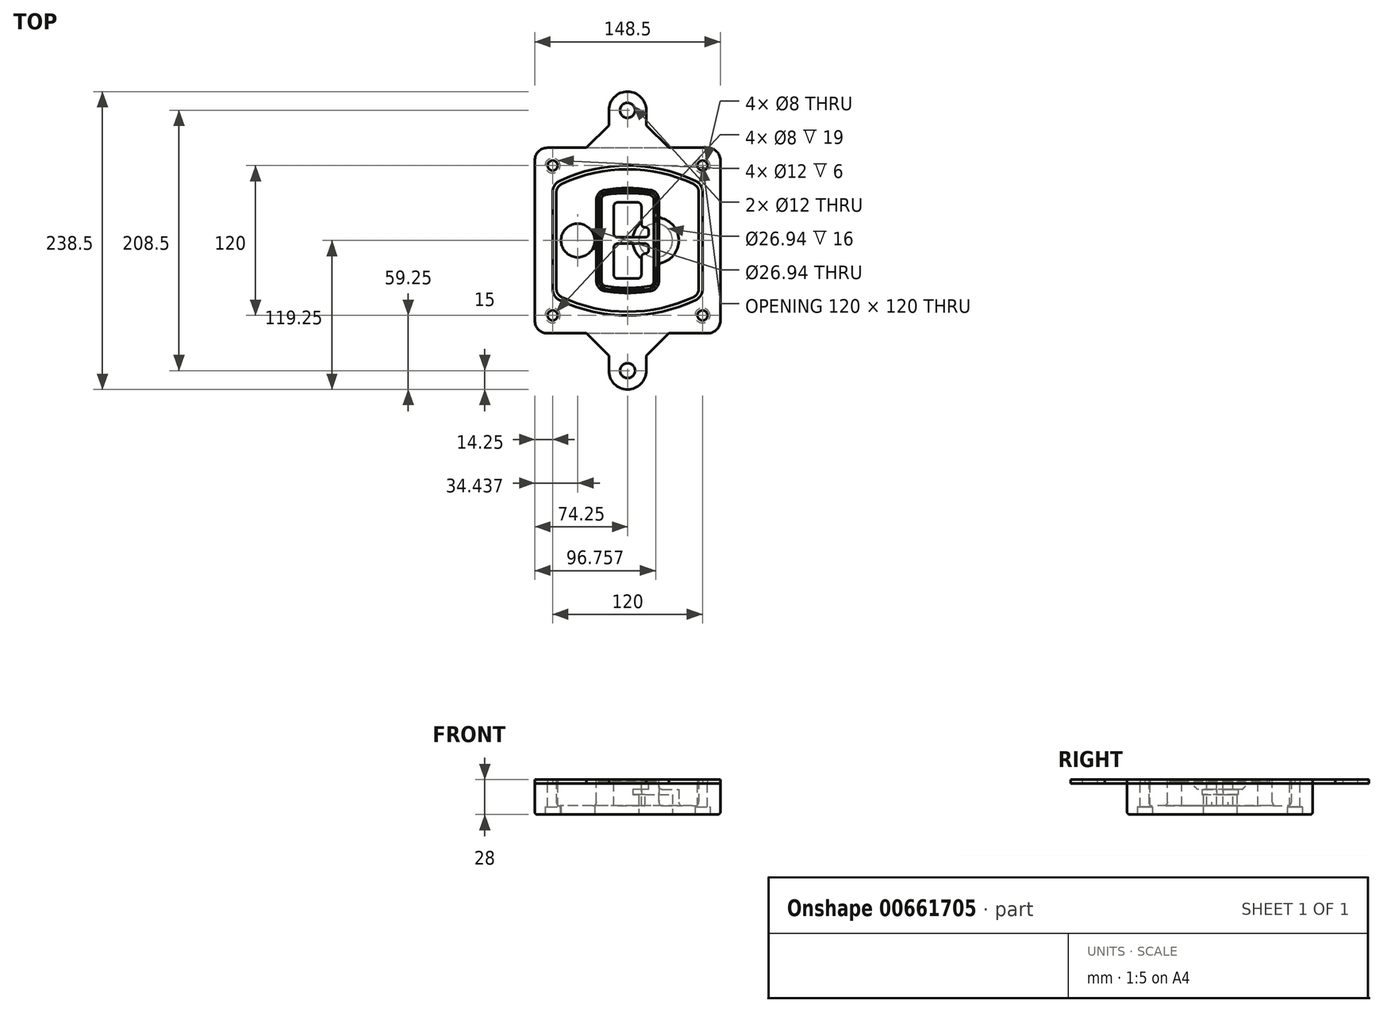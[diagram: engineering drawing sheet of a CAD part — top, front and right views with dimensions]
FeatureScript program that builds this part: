
annotation { "Feature Type Name" : "Feature", "Feature Type Description" : "" }
export const myFeature = defineFeature(function(context is Context, id is Id, definition is map)
    precondition{}
    {
        {
            var Q0;
            Q0=qCreatedBy(makeId("Top.planeOp"),FACE);
            var sketch = newSketch(context, id + "F0", { "sketchPlane" : qUnion([Q0])});
            skPoint(sketch, "E0.rect.middle", {"position": v(0, 0) * mm});
            skLineSegment(sketch, "E1.bottom", {"start": v(-64.25, -74.25) * mm, "end": v(64.25, -74.25) * mm});
            skLineSegment(sketch, "E1.top", {"start": v(-64.25, 74.25) * mm, "end": v(64.25, 74.25) * mm});
            skLineSegment(sketch, "E1.left", {"start": v(-74.25, -64.25) * mm, "end": v(-74.25, 64.25) * mm});
            skLineSegment(sketch, "E1.right", {"start": v(74.25, -64.25) * mm, "end": v(74.25, 64.25) * mm});
            skLineSegment(sketch, "E2", {"start": v(-74.25, 74.25) * mm, "end": v(74.25, -74.25) * mm, "construction": true});
            skLineSegment(sketch, "E3", {"start": v(74.25, 74.25) * mm, "end": v(-74.25, -74.25) * mm, "construction": true});
            skCircle(sketch, "E4", {"center": v(-60, 60) * mm, "radius": 4 * mm});
            skCircle(sketch, "E5", {"center": v(60, 60) * mm, "radius": 4 * mm});
            skCircle(sketch, "E6", {"center": v(60, -60) * mm, "radius": 4 * mm});
            skCircle(sketch, "E7", {"center": v(-60, -60) * mm, "radius": 4 * mm});
            skLineSegment(sketch, "E8", {"start": v(-60, 60) * mm, "end": v(60, 60) * mm, "construction": true});
            skLineSegment(sketch, "E9", {"start": v(60, 60) * mm, "end": v(60, -60) * mm, "construction": true});
            skLineSegment(sketch, "E10", {"start": v(60, -60) * mm, "end": v(-60, -60) * mm, "construction": true});
            skLineSegment(sketch, "E11", {"start": v(-60, -60) * mm, "end": v(-60, 60) * mm, "construction": true});
            skLineSegment(sketch, "E12", {"start": v(-60, 38.83) * mm, "end": v(-60, -38.83) * mm});
            skLineSegment(sketch, "E13", {"start": v(60, 38.83) * mm, "end": v(60, -38.83) * mm});
            skArc(sketch, "E14", {"start": v(54.26, 47.88) * mm, "mid": v(0, 60) * mm, "end": v(-54.26, 47.88) * mm});
            skArc(sketch, "E15", {"start": v(-54.26, -47.88) * mm, "mid": v(0, -60) * mm, "end": v(54.26, -47.88) * mm});
            skLineSegment(sketch, "E16", {"start": v(-60, 0) * mm, "end": v(60, 0) * mm, "construction": true});
            skPoint(sketch, "E17.visualSharp", {"position": v(-60, -45) * mm});
            skArc(sketch, "E17.filletArc", {"start": v(-60, -38.83) * mm, "mid": v(-58.44, -44.2) * mm, "end": v(-54.26, -47.88) * mm});
            skPoint(sketch, "E18.visualSharp", {"position": v(-60, 45) * mm});
            skArc(sketch, "E18.filletArc", {"start": v(-54.26, 47.88) * mm, "mid": v(-58.44, 44.2) * mm, "end": v(-60, 38.83) * mm});
            skPoint(sketch, "E19.visualSharp", {"position": v(60, 45) * mm});
            skArc(sketch, "E19.filletArc", {"start": v(60, 38.83) * mm, "mid": v(58.44, 44.2) * mm, "end": v(54.26, 47.88) * mm});
            skPoint(sketch, "E20.visualSharp", {"position": v(60, -45) * mm});
            skArc(sketch, "E20.filletArc", {"start": v(54.26, -47.88) * mm, "mid": v(58.44, -44.2) * mm, "end": v(60, -38.83) * mm});
            skPoint(sketch, "E21.visualSharp", {"position": v(-74.25, 74.25) * mm});
            skArc(sketch, "E21.filletArc", {"start": v(-64.25, 74.25) * mm, "mid": v(-71.32, 71.32) * mm, "end": v(-74.25, 64.25) * mm});
            skPoint(sketch, "E22.visualSharp", {"position": v(74.25, 74.25) * mm});
            skArc(sketch, "E22.filletArc", {"start": v(74.25, 64.25) * mm, "mid": v(71.32, 71.32) * mm, "end": v(64.25, 74.25) * mm});
            skPoint(sketch, "E23.visualSharp", {"position": v(74.25, -74.25) * mm});
            skArc(sketch, "E23.filletArc", {"start": v(64.25, -74.25) * mm, "mid": v(71.32, -71.32) * mm, "end": v(74.25, -64.25) * mm});
            skPoint(sketch, "E24.visualSharp", {"position": v(-74.25, -74.25) * mm});
            skArc(sketch, "E24.filletArc", {"start": v(-74.25, -64.25) * mm, "mid": v(-71.32, -71.32) * mm, "end": v(-64.25, -74.25) * mm});
            skArc(sketch, "E25.0", {"start": v(57, 38.83) * mm, "mid": v(55.9, 42.58) * mm, "end": v(52.98, 45.17) * mm});
            skLineSegment(sketch, "E25.1", {"start": v(57, 38.83) * mm, "end": v(57, -38.83) * mm});
            skArc(sketch, "E25.2", {"start": v(52.98, -45.17) * mm, "mid": v(55.9, -42.58) * mm, "end": v(57, -38.83) * mm});
            skArc(sketch, "E25.3", {"start": v(-52.98, -45.17) * mm, "mid": v(0, -57) * mm, "end": v(52.98, -45.17) * mm});
            skArc(sketch, "E25.4", {"start": v(-57, -38.83) * mm, "mid": v(-55.9, -42.58) * mm, "end": v(-52.98, -45.17) * mm});
            skArc(sketch, "E25.5", {"start": v(52.98, 45.17) * mm, "mid": v(0, 57) * mm, "end": v(-52.98, 45.17) * mm});
            skLineSegment(sketch, "E25.6", {"start": v(-57, 38.83) * mm, "end": v(-57, -38.83) * mm});
            skArc(sketch, "E25.7", {"start": v(-52.98, 45.17) * mm, "mid": v(-55.9, 42.58) * mm, "end": v(-57, 38.83) * mm});
            skArc(sketch, "E26.0", {"start": v(-55.96, 51.5) * mm, "mid": v(-61.82, 46.33) * mm, "end": v(-64, 38.83) * mm});
            skArc(sketch, "E26.1", {"start": v(55.96, 51.5) * mm, "mid": v(0, 64) * mm, "end": v(-55.96, 51.5) * mm});
            skArc(sketch, "E26.2", {"start": v(64, 38.83) * mm, "mid": v(61.82, 46.33) * mm, "end": v(55.96, 51.5) * mm});
            skLineSegment(sketch, "E26.3", {"start": v(64, 38.83) * mm, "end": v(64, -38.83) * mm});
            skArc(sketch, "E26.4", {"start": v(55.96, -51.5) * mm, "mid": v(61.82, -46.33) * mm, "end": v(64, -38.83) * mm});
            skLineSegment(sketch, "E26.5", {"start": v(-64, 38.83) * mm, "end": v(-64, -38.83) * mm});
            skArc(sketch, "E26.6", {"start": v(-55.96, -51.5) * mm, "mid": v(0, -64) * mm, "end": v(55.96, -51.5) * mm});
            skArc(sketch, "E26.7", {"start": v(-64, -38.83) * mm, "mid": v(-61.82, -46.33) * mm, "end": v(-55.96, -51.5) * mm});
            skSolve(sketch);
        }
        {
            var Q0;
            Q0=makeQuery(id+"F0.imprint","IMPRINT",FACE,{"disambiguationData":[TD([[makeQuery(id+"F0.imprint","IMPRINT",EDGE,{"derivedFrom":sQuery(id+"F0.wireOp",EDGE,"E1.bottom")}),1.0]])]});
            var Q1;
            Q1=makeQuery(id+"F0.imprint","IMPRINT",FACE,{"disambiguationData":[TD([[makeQuery(id+"F0.imprint","IMPRINT",EDGE,{"derivedFrom":sQuery(id+"F0.wireOp",EDGE,"E12")}),1.0]])]});
            var Q2;
            Q2=makeQuery(id+"F0.imprint","IMPRINT",FACE,{"disambiguationData":[TD([[makeQuery(id+"F0.imprint","IMPRINT",EDGE,{"derivedFrom":sQuery(id+"F0.wireOp",EDGE,"E25.0")}),1.0]])]});
            var Q3;
            Q3=makeQuery(id+"F0.imprint","IMPRINT",FACE,{"disambiguationData":[TD([[makeQuery(id+"F0.imprint","IMPRINT",EDGE,{"derivedFrom":sQuery(id+"F0.wireOp",EDGE,"E12")}),-1.0]])]});
            extrude(context, id + "F1", {"entities" : qUnion([Q0, Q1, Q2, Q3]), "oppositeDirection" : true, "depth" : 25 * mm});
        }
        {
            var Q0;
            Q0=makeQuery(id+"F0.imprint","IMPRINT",FACE,{"disambiguationData":[TD([[makeQuery(id+"F0.imprint","IMPRINT",EDGE,{"derivedFrom":sQuery(id+"F0.wireOp",EDGE,"E12")}),1.0]])]});
            extrude(context, id + "F2", {"entities" : qUnion([Q0]), "operationType" : NewBodyOperationType.ADD, "depth" : 3 * mm});
        }
        {
            var Q0;
            Q0=makeQuery(id+"F0.imprint","IMPRINT",FACE,{"disambiguationData":[TD([[makeQuery(id+"F0.imprint","IMPRINT",EDGE,{"derivedFrom":sQuery(id+"F0.wireOp",EDGE,"E25.0")}),1.0]])]});
            extrude(context, id + "F3", {"entities" : qUnion([Q0]), "operationType" : NewBodyOperationType.REMOVE, "oppositeDirection" : true, "depth" : 18 * mm});
        }
        {
            var Q0;
            Q0=makeQuery(id+"F2.opExtrude","CAP_FACE",FACE,{"disambiguationData":[OSD([sQuery(id+"F0.wireOp",EDGE,"E12"),sQuery(id+"F0.wireOp",EDGE,"E13"),sQuery(id+"F0.wireOp",EDGE,"E14"),sQuery(id+"F0.wireOp",EDGE,"E15"),sQuery(id+"F0.wireOp",EDGE,"E17.filletArc"),sQuery(id+"F0.wireOp",EDGE,"E18.filletArc"),sQuery(id+"F0.wireOp",EDGE,"E19.filletArc"),sQuery(id+"F0.wireOp",EDGE,"E20.filletArc"),sQuery(id+"F0.wireOp",EDGE,"E25.0"),sQuery(id+"F0.wireOp",EDGE,"E25.1"),sQuery(id+"F0.wireOp",EDGE,"E25.2"),sQuery(id+"F0.wireOp",EDGE,"E25.3"),sQuery(id+"F0.wireOp",EDGE,"E25.4"),sQuery(id+"F0.wireOp",EDGE,"E25.5"),sQuery(id+"F0.wireOp",EDGE,"E25.6"),sQuery(id+"F0.wireOp",EDGE,"E25.7")])],"isStart":false});
            var sketch = newSketch(context, id + "F4", { "sketchPlane" : qUnion([Q0])});
            skArc(sketch, "E27.0", {"start": v(-18.34, -40.45) * mm, "mid": v(0, -42) * mm, "end": v(18.34, -40.45) * mm});
            skArc(sketch, "E28.0", {"start": v(18.34, 40.45) * mm, "mid": v(0, 42) * mm, "end": v(-18.34, 40.45) * mm});
            skLineSegment(sketch, "E29", {"start": v(-25, 32.57) * mm, "end": v(-25, -32.57) * mm});
            skLineSegment(sketch, "E30", {"start": v(25, 32.57) * mm, "end": v(25, -32.57) * mm});
            skLineSegment(sketch, "E31", {"start": v(-25, 39.1) * mm, "end": v(25, 39.1) * mm, "construction": true});
            skLineSegment(sketch, "E32", {"start": v(-25, -39.1) * mm, "end": v(25, -39.1) * mm, "construction": true});
            skPoint(sketch, "E33.visualSharp", {"position": v(-25, 39.1) * mm});
            skArc(sketch, "E33.filletArc", {"start": v(-18.34, 40.45) * mm, "mid": v(-23.11, 37.73) * mm, "end": v(-25, 32.57) * mm});
            skPoint(sketch, "E34.visualSharp", {"position": v(25, 39.1) * mm});
            skArc(sketch, "E34.filletArc", {"start": v(25, 32.57) * mm, "mid": v(23.11, 37.73) * mm, "end": v(18.34, 40.45) * mm});
            skPoint(sketch, "E35.visualSharp", {"position": v(25, -39.1) * mm});
            skArc(sketch, "E35.filletArc", {"start": v(18.34, -40.45) * mm, "mid": v(23.11, -37.73) * mm, "end": v(25, -32.57) * mm});
            skPoint(sketch, "E36.visualSharp", {"position": v(-25, -39.1) * mm});
            skArc(sketch, "E36.filletArc", {"start": v(-25, -32.57) * mm, "mid": v(-23.11, -37.73) * mm, "end": v(-18.34, -40.45) * mm});
            skArc(sketch, "E37.0", {"start": v(52.98, 45.17) * mm, "mid": v(0, 57) * mm, "end": v(-52.98, 45.17) * mm});
            skArc(sketch, "E37.1", {"start": v(-52.98, 45.17) * mm, "mid": v(-55.9, 42.58) * mm, "end": v(-57, 38.83) * mm});
            skLineSegment(sketch, "E37.2", {"start": v(-57, 38.83) * mm, "end": v(-57, -38.83) * mm});
            skArc(sketch, "E37.3", {"start": v(-57, -38.83) * mm, "mid": v(-55.9, -42.58) * mm, "end": v(-52.98, -45.17) * mm});
            skArc(sketch, "E37.4", {"start": v(-52.98, -45.17) * mm, "mid": v(0, -57) * mm, "end": v(52.98, -45.17) * mm});
            skArc(sketch, "E37.5", {"start": v(52.98, -45.17) * mm, "mid": v(55.9, -42.58) * mm, "end": v(57, -38.83) * mm});
            skLineSegment(sketch, "E37.6", {"start": v(57, 38.83) * mm, "end": v(57, -38.83) * mm});
            skArc(sketch, "E37.7", {"start": v(57, 38.83) * mm, "mid": v(55.9, 42.58) * mm, "end": v(52.98, 45.17) * mm});
            skLineSegment(sketch, "E38.0", {"start": v(23, 32.57) * mm, "end": v(23, -32.57) * mm});
            skArc(sketch, "E38.1", {"start": v(18, -38.48) * mm, "mid": v(21.58, -36.44) * mm, "end": v(23, -32.57) * mm});
            skArc(sketch, "E38.2", {"start": v(-18, -38.48) * mm, "mid": v(0, -40) * mm, "end": v(18, -38.48) * mm});
            skArc(sketch, "E38.3", {"start": v(-23, -32.57) * mm, "mid": v(-21.58, -36.44) * mm, "end": v(-18, -38.48) * mm});
            skLineSegment(sketch, "E38.4", {"start": v(-23, 32.57) * mm, "end": v(-23, -32.57) * mm});
            skArc(sketch, "E38.5", {"start": v(23, 32.57) * mm, "mid": v(21.58, 36.44) * mm, "end": v(18, 38.48) * mm});
            skArc(sketch, "E38.6", {"start": v(-18, 38.48) * mm, "mid": v(-21.58, 36.44) * mm, "end": v(-23, 32.57) * mm});
            skArc(sketch, "E38.7", {"start": v(18, 38.48) * mm, "mid": v(0, 40) * mm, "end": v(-18, 38.48) * mm});
            skArc(sketch, "E39.0", {"start": v(21, 32.57) * mm, "mid": v(20.06, 35.15) * mm, "end": v(17.67, 36.5) * mm});
            skLineSegment(sketch, "E39.1", {"start": v(21, 32.57) * mm, "end": v(21, -32.57) * mm});
            skArc(sketch, "E39.2", {"start": v(17.67, -36.5) * mm, "mid": v(20.06, -35.15) * mm, "end": v(21, -32.57) * mm});
            skArc(sketch, "E39.3", {"start": v(-17.67, -36.5) * mm, "mid": v(0, -38) * mm, "end": v(17.67, -36.5) * mm});
            skArc(sketch, "E39.4", {"start": v(-21, -32.57) * mm, "mid": v(-20.06, -35.15) * mm, "end": v(-17.67, -36.5) * mm});
            skArc(sketch, "E39.5", {"start": v(17.67, 36.5) * mm, "mid": v(0, 38) * mm, "end": v(-17.67, 36.5) * mm});
            skLineSegment(sketch, "E39.6", {"start": v(-21, 32.57) * mm, "end": v(-21, -32.57) * mm});
            skArc(sketch, "E39.7", {"start": v(-17.67, 36.5) * mm, "mid": v(-20.06, 35.15) * mm, "end": v(-21, 32.57) * mm});
            skLineSegment(sketch, "E40", {"start": v(-25, 0) * mm, "end": v(25, 0) * mm, "construction": true});
            skLineSegment(sketch, "E41", {"start": v(-11, 5.5) * mm, "end": v(-11, 27.5) * mm});
            skLineSegment(sketch, "E42", {"start": v(-8, 30.5) * mm, "end": v(8, 30.5) * mm});
            skLineSegment(sketch, "E43", {"start": v(11, 27.5) * mm, "end": v(11, 13.5) * mm});
            skLineSegment(sketch, "E44", {"start": v(14, 10.5) * mm, "end": v(14, 10.5) * mm});
            skLineSegment(sketch, "E45", {"start": v(17, 7.5) * mm, "end": v(17, 5.5) * mm});
            skLineSegment(sketch, "E46", {"start": v(14, 2.5) * mm, "end": v(-8, 2.5) * mm});
            skPoint(sketch, "E47.visualSharp", {"position": v(-11, 30.5) * mm});
            skArc(sketch, "E47.filletArc", {"start": v(-8, 30.5) * mm, "mid": v(-10.12, 29.62) * mm, "end": v(-11, 27.5) * mm});
            skPoint(sketch, "E48.visualSharp", {"position": v(11, 30.5) * mm});
            skArc(sketch, "E48.filletArc", {"start": v(11, 27.5) * mm, "mid": v(10.12, 29.62) * mm, "end": v(8, 30.5) * mm});
            skPoint(sketch, "E49.visualSharp", {"position": v(11, 10.5) * mm});
            skArc(sketch, "E49.filletArc", {"start": v(11, 13.5) * mm, "mid": v(11.88, 11.38) * mm, "end": v(14, 10.5) * mm});
            skPoint(sketch, "E50.visualSharp", {"position": v(17, 10.5) * mm});
            skArc(sketch, "E50.filletArc", {"start": v(17, 7.5) * mm, "mid": v(16.12, 9.62) * mm, "end": v(14, 10.5) * mm});
            skPoint(sketch, "E51.visualSharp", {"position": v(17, 2.5) * mm});
            skArc(sketch, "E51.filletArc", {"start": v(14, 2.5) * mm, "mid": v(16.12, 3.38) * mm, "end": v(17, 5.5) * mm});
            skPoint(sketch, "E52.visualSharp", {"position": v(-11, 2.5) * mm});
            skArc(sketch, "E52.filletArc", {"start": v(-11, 5.5) * mm, "mid": v(-10.12, 3.38) * mm, "end": v(-8, 2.5) * mm});
            skLineSegment(sketch, "E53.0.MirrorCS", {"start": v(14, -2.5) * mm, "end": v(-8, -2.5) * mm});
            skArc(sketch, "E54.0.MirrorCS", {"start": v(-11, -5.5) * mm, "mid": v(-10.12, -3.38) * mm, "end": v(-8, -2.5) * mm});
            skLineSegment(sketch, "E55.0.MirrorCS", {"start": v(-11, -5.5) * mm, "end": v(-11, -27.5) * mm});
            skArc(sketch, "E56.0.MirrorCS", {"start": v(-8, -30.5) * mm, "mid": v(-10.12, -29.62) * mm, "end": v(-11, -27.5) * mm});
            skLineSegment(sketch, "E57.0.MirrorCS", {"start": v(-8, -30.5) * mm, "end": v(8, -30.5) * mm});
            skArc(sketch, "E58.0.MirrorCS", {"start": v(11, -27.5) * mm, "mid": v(10.12, -29.62) * mm, "end": v(8, -30.5) * mm});
            skLineSegment(sketch, "E59.0.MirrorCS", {"start": v(11, -27.5) * mm, "end": v(11, -13.5) * mm});
            skArc(sketch, "E60.0.MirrorCS", {"start": v(11, -13.5) * mm, "mid": v(11.88, -11.38) * mm, "end": v(14, -10.5) * mm});
            skArc(sketch, "E61.0.MirrorCS", {"start": v(17, -7.5) * mm, "mid": v(16.12, -9.62) * mm, "end": v(14, -10.5) * mm});
            skLineSegment(sketch, "E62.0.MirrorCS", {"start": v(17, -7.5) * mm, "end": v(17, -5.5) * mm});
            skArc(sketch, "E63.0.MirrorCS", {"start": v(14, -2.5) * mm, "mid": v(16.12, -3.38) * mm, "end": v(17, -5.5) * mm});
            skSolve(sketch);
        }
        {
            var Q0;
            Q0=makeQuery(id+"F4.imprint","IMPRINT",FACE,{"disambiguationData":[TD([[makeQuery(id+"F4.imprint","IMPRINT",EDGE,{"derivedFrom":sQuery(id+"F4.wireOp",EDGE,"E27.0")}),1.0]])]});
            var Q1;
            Q1=makeQuery(id+"F4.imprint","IMPRINT",FACE,{"disambiguationData":[TD([[makeQuery(id+"F4.imprint","IMPRINT",EDGE,{"derivedFrom":sQuery(id+"F4.wireOp",EDGE,"E38.0")}),-1.0]])]});
            var Q2;
            Q2=makeQuery(id+"F4.imprint","IMPRINT",FACE,{"disambiguationData":[TD([[makeQuery(id+"F4.imprint","IMPRINT",EDGE,{"derivedFrom":sQuery(id+"F4.wireOp",EDGE,"E39.0")}),1.0]])]});
            extrude(context, id + "F5", {"entities" : qUnion([Q0, Q1, Q2]), "operationType" : NewBodyOperationType.ADD, "endBound" : BoundingType.UP_TO_NEXT, "oppositeDirection" : true, "depth" : 25 * mm});
        }
        {
            var Q0;
            Q0=makeQuery(id+"F4.imprint","IMPRINT",FACE,{"disambiguationData":[TD([[makeQuery(id+"F4.imprint","IMPRINT",EDGE,{"derivedFrom":sQuery(id+"F4.wireOp",EDGE,"E38.0")}),-1.0]])]});
            extrude(context, id + "F6", {"entities" : qUnion([Q0]), "operationType" : NewBodyOperationType.REMOVE, "oppositeDirection" : true, "depth" : 2 * mm});
        }
        {
            var Q0;
            Q0=makeQuery(id+"F1.opExtrude","CAP_FACE",FACE,{"disambiguationData":[OSD([sQuery(id+"F0.wireOp",EDGE,"E1.bottom"),sQuery(id+"F0.wireOp",EDGE,"E1.top"),sQuery(id+"F0.wireOp",EDGE,"E1.left"),sQuery(id+"F0.wireOp",EDGE,"E1.right"),sQuery(id+"F0.wireOp",EDGE,"E4"),sQuery(id+"F0.wireOp",EDGE,"E5"),sQuery(id+"F0.wireOp",EDGE,"E6"),sQuery(id+"F0.wireOp",EDGE,"E7"),sQuery(id+"F0.wireOp",EDGE,"E21.filletArc"),sQuery(id+"F0.wireOp",EDGE,"E22.filletArc"),sQuery(id+"F0.wireOp",EDGE,"E23.filletArc"),sQuery(id+"F0.wireOp",EDGE,"E24.filletArc")])],"isStart":false});
            var sketch = newSketch(context, id + "F7", { "sketchPlane" : qUnion([Q0])});
            skCircle(sketch, "E64", {"center": v(22.5, 0) * mm, "radius": 13.47 * mm});
            skCircle(sketch, "E65", {"center": v(-39.81, 0) * mm, "radius": 13.47 * mm});
            skLineSegment(sketch, "E66", {"start": v(74.25, 0) * mm, "end": v(-74.25, 0) * mm});
            skCircle(sketch, "E67", {"center": v(22.5, 0) * mm, "radius": 18.47 * mm});
            skCircle(sketch, "E68", {"center": v(60, -60) * mm, "radius": 6 * mm});
            skCircle(sketch, "E69", {"center": v(-60, -60) * mm, "radius": 6 * mm});
            skCircle(sketch, "E70", {"center": v(-60, 60) * mm, "radius": 6 * mm});
            skCircle(sketch, "E71", {"center": v(60, 60) * mm, "radius": 6 * mm});
            skSolve(sketch);
        }
        {
            var Q0;
            {var subQ1=sQuery(id+"F7.wireOp",EDGE,"E66");var subQ4=sQuery(id+"F7.wireOp",EDGE,"E64");var subQ6=makeQuery(id+"F7.imprint","INTERSECT",VERTEX,{"disambiguationData":[OD(0.0)],"derivedFrom":[subQ4,subQ1]});Q0=makeQuery(id+"F7.imprint","IMPRINT",FACE,{"disambiguationData":[TD([[makeQuery(id+"F7.imprint","IMPRINT",EDGE,{"disambiguationData":[TD([[subQ6,-1.0]])],"derivedFrom":subQ4}),-1.0]])]});}
            var Q1;
            {var subQ0=sQuery(id+"F7.wireOp",EDGE,"E66");var subQ1=sQuery(id+"F7.wireOp",EDGE,"E64");var subQ3=makeQuery(id+"F7.imprint","INTERSECT",VERTEX,{"disambiguationData":[OD(0.0)],"derivedFrom":[subQ1,subQ0]});Q1=makeQuery(id+"F7.imprint","IMPRINT",FACE,{"disambiguationData":[TD([[makeQuery(id+"F7.imprint","IMPRINT",EDGE,{"disambiguationData":[TD([[subQ3,-1.0]])],"derivedFrom":subQ1}),1.0]])]});}
            var Q2;
            {var subQ0=sQuery(id+"F7.wireOp",EDGE,"E66");var subQ1=sQuery(id+"F7.wireOp",EDGE,"E64");var subQ3=makeQuery(id+"F7.imprint","INTERSECT",VERTEX,{"disambiguationData":[OD(0.0)],"derivedFrom":[subQ1,subQ0]});Q2=makeQuery(id+"F7.imprint","IMPRINT",FACE,{"disambiguationData":[TD([[makeQuery(id+"F7.imprint","IMPRINT",EDGE,{"disambiguationData":[TD([[subQ3,1.0]])],"derivedFrom":subQ1}),1.0]])]});}
            var Q3;
            {var subQ1=sQuery(id+"F7.wireOp",EDGE,"E66");var subQ4=sQuery(id+"F7.wireOp",EDGE,"E64");var subQ6=makeQuery(id+"F7.imprint","INTERSECT",VERTEX,{"disambiguationData":[OD(0.0)],"derivedFrom":[subQ4,subQ1]});Q3=makeQuery(id+"F7.imprint","IMPRINT",FACE,{"disambiguationData":[TD([[makeQuery(id+"F7.imprint","IMPRINT",EDGE,{"disambiguationData":[TD([[subQ6,1.0]])],"derivedFrom":subQ4}),-1.0]])]});}
            extrude(context, id + "F8", {"entities" : qUnion([Q0, Q1, Q2, Q3]), "operationType" : NewBodyOperationType.ADD, "oppositeDirection" : true, "depth" : 20 * mm});
        }
        {
            var Q0;
            {var subQ0=sQuery(id+"F7.wireOp",EDGE,"E66");var subQ1=sQuery(id+"F7.wireOp",EDGE,"E64");var subQ3=makeQuery(id+"F7.imprint","INTERSECT",VERTEX,{"disambiguationData":[OD(0.0)],"derivedFrom":[subQ1,subQ0]});Q0=makeQuery(id+"F7.imprint","IMPRINT",FACE,{"disambiguationData":[TD([[makeQuery(id+"F7.imprint","IMPRINT",EDGE,{"disambiguationData":[TD([[subQ3,-1.0]])],"derivedFrom":subQ1}),1.0]])]});}
            var Q1;
            {var subQ0=sQuery(id+"F7.wireOp",EDGE,"E66");var subQ1=sQuery(id+"F7.wireOp",EDGE,"E64");var subQ3=makeQuery(id+"F7.imprint","INTERSECT",VERTEX,{"disambiguationData":[OD(0.0)],"derivedFrom":[subQ1,subQ0]});Q1=makeQuery(id+"F7.imprint","IMPRINT",FACE,{"disambiguationData":[TD([[makeQuery(id+"F7.imprint","IMPRINT",EDGE,{"disambiguationData":[TD([[subQ3,1.0]])],"derivedFrom":subQ1}),1.0]])]});}
            var Q2;
            Q2 = qSketchRegion(id + "F16", true);
            extrude(context, id + "F9", {"entities" : qUnion([Q0, Q1, Q2]), "operationType" : NewBodyOperationType.REMOVE, "oppositeDirection" : true, "depth" : 16 * mm, "offsetDistance" : 25 * mm});
        }
        {
            var Q0;
            {var subQ0=sQuery(id+"F7.wireOp",EDGE,"E66");var subQ1=sQuery(id+"F7.wireOp",EDGE,"E65");var subQ3=makeQuery(id+"F7.imprint","INTERSECT",VERTEX,{"disambiguationData":[OD(0.0)],"derivedFrom":[subQ1,subQ0]});Q0=makeQuery(id+"F7.imprint","IMPRINT",FACE,{"disambiguationData":[TD([[makeQuery(id+"F7.imprint","IMPRINT",EDGE,{"disambiguationData":[TD([[subQ3,-1.0]])],"derivedFrom":subQ1}),1.0]])]});}
            var Q1;
            {var subQ0=sQuery(id+"F7.wireOp",EDGE,"E66");var subQ1=sQuery(id+"F7.wireOp",EDGE,"E65");var subQ3=makeQuery(id+"F7.imprint","INTERSECT",VERTEX,{"disambiguationData":[OD(0.0)],"derivedFrom":[subQ1,subQ0]});Q1=makeQuery(id+"F7.imprint","IMPRINT",FACE,{"disambiguationData":[TD([[makeQuery(id+"F7.imprint","IMPRINT",EDGE,{"disambiguationData":[TD([[subQ3,1.0]])],"derivedFrom":subQ1}),1.0]])]});}
            extrude(context, id + "F10", {"entities" : qUnion([Q0, Q1]), "operationType" : NewBodyOperationType.REMOVE, "oppositeDirection" : true, "depth" : 25 * mm});
        }
        {
            var Q0;
            Q0=makeQuery(id+"F7.imprint","IMPRINT",FACE,{"disambiguationData":[TD([[makeQuery(id+"F7.imprint","IMPRINT",EDGE,{"derivedFrom":sQuery(id+"F7.wireOp",EDGE,"E68")}),1.0]])]});
            var Q1;
            Q1=makeQuery(id+"F7.imprint","IMPRINT",FACE,{"disambiguationData":[TD([[makeQuery(id+"F7.imprint","IMPRINT",EDGE,{"derivedFrom":makeQuery(id+"F1.opExtrude","CAP_EDGE",EDGE,{"disambiguationData":[OSD([sQuery(id+"F0.wireOp",EDGE,"E5")])],"isStart":false})}),-1.0]])]});
            var Q2;
            Q2=makeQuery(id+"F7.imprint","IMPRINT",FACE,{"disambiguationData":[TD([[makeQuery(id+"F7.imprint","IMPRINT",EDGE,{"derivedFrom":sQuery(id+"F7.wireOp",EDGE,"E69")}),1.0]])]});
            var Q3;
            Q3=makeQuery(id+"F7.imprint","IMPRINT",FACE,{"disambiguationData":[TD([[makeQuery(id+"F7.imprint","IMPRINT",EDGE,{"derivedFrom":makeQuery(id+"F1.opExtrude","CAP_EDGE",EDGE,{"disambiguationData":[OSD([sQuery(id+"F0.wireOp",EDGE,"E4")])],"isStart":false})}),-1.0]])]});
            var Q4;
            Q4=makeQuery(id+"F7.imprint","IMPRINT",FACE,{"disambiguationData":[TD([[makeQuery(id+"F7.imprint","IMPRINT",EDGE,{"derivedFrom":sQuery(id+"F7.wireOp",EDGE,"E70")}),1.0]])]});
            var Q5;
            Q5=makeQuery(id+"F7.imprint","IMPRINT",FACE,{"disambiguationData":[TD([[makeQuery(id+"F7.imprint","IMPRINT",EDGE,{"derivedFrom":makeQuery(id+"F1.opExtrude","CAP_EDGE",EDGE,{"disambiguationData":[OSD([sQuery(id+"F0.wireOp",EDGE,"E7")])],"isStart":false})}),-1.0]])]});
            var Q6;
            Q6=makeQuery(id+"F7.imprint","IMPRINT",FACE,{"disambiguationData":[TD([[makeQuery(id+"F7.imprint","IMPRINT",EDGE,{"derivedFrom":sQuery(id+"F7.wireOp",EDGE,"E71")}),1.0]])]});
            var Q7;
            Q7=makeQuery(id+"F7.imprint","IMPRINT",FACE,{"disambiguationData":[TD([[makeQuery(id+"F7.imprint","IMPRINT",EDGE,{"derivedFrom":makeQuery(id+"F1.opExtrude","CAP_EDGE",EDGE,{"disambiguationData":[OSD([sQuery(id+"F0.wireOp",EDGE,"E6")])],"isStart":false})}),-1.0]])]});
            extrude(context, id + "F11", {"entities" : qUnion([Q0, Q1, Q2, Q3, Q4, Q5, Q6, Q7]), "operationType" : NewBodyOperationType.REMOVE, "oppositeDirection" : true, "depth" : 6 * mm});
        }
        {
            var Q0;
            Q0=makeQuery(id+"F9.boolean.opBoolean","COPY",FACE,{"derivedFrom":makeQuery(id+"F9.opExtrude","CAP_FACE",FACE,{"disambiguationData":[OSD([sQuery(id+"F7.wireOp",EDGE,"E64")])],"isStart":false})});
            var sketch = newSketch(context, id + "F12", { "sketchPlane" : qUnion([Q0])});
            skArc(sketch, "E72.0", {"start": v(11, 14.45) * mm, "mid": v(6.45, 9.13) * mm, "end": v(4.2, 2.5) * mm});
            skArc(sketch, "E72.1", {"start": v(4.2, -2.5) * mm, "mid": v(6.45, -9.13) * mm, "end": v(11, -14.45) * mm});
            skLineSegment(sketch, "E73", {"start": v(4.2, -2.5) * mm, "end": v(14, -2.5) * mm});
            skLineSegment(sketch, "E74.0", {"start": v(14, 2.5) * mm, "end": v(4.2, 2.5) * mm});
            skArc(sketch, "E74.1", {"start": v(14, 2.5) * mm, "mid": v(16.12, 3.38) * mm, "end": v(17, 5.5) * mm});
            skLineSegment(sketch, "E74.2", {"start": v(17, 7.5) * mm, "end": v(17, 5.5) * mm});
            skArc(sketch, "E74.3", {"start": v(17, 7.5) * mm, "mid": v(16.12, 9.62) * mm, "end": v(14, 10.5) * mm});
            skArc(sketch, "E74.4", {"start": v(11, 13.5) * mm, "mid": v(11.88, 11.38) * mm, "end": v(14, 10.5) * mm});
            skLineSegment(sketch, "E74.5", {"start": v(11, 14.45) * mm, "end": v(11, 13.5) * mm});
            skLineSegment(sketch, "E74.7", {"start": v(14, -2.5) * mm, "end": v(4.2, -2.5) * mm});
            skArc(sketch, "E74.8", {"start": v(14, -2.5) * mm, "mid": v(16.12, -3.38) * mm, "end": v(17, -5.5) * mm});
            skLineSegment(sketch, "E74.9", {"start": v(17, -7.5) * mm, "end": v(17, -5.5) * mm});
            skArc(sketch, "E74.10", {"start": v(17, -7.5) * mm, "mid": v(16.12, -9.62) * mm, "end": v(14, -10.5) * mm});
            skArc(sketch, "E74.11", {"start": v(11, -13.5) * mm, "mid": v(11.88, -11.38) * mm, "end": v(14, -10.5) * mm});
            skLineSegment(sketch, "E74.12", {"start": v(11, -14.45) * mm, "end": v(11, -13.5) * mm});
            skPoint(sketch, "E75.orphan", {"position": v(11, -27.5) * mm});
            skPoint(sketch, "E76.orphan", {"position": v(-8, -2.5) * mm});
            skPoint(sketch, "E77.orphan", {"position": v(-8, 2.5) * mm});
            skPoint(sketch, "E78.orphan", {"position": v(11, 27.5) * mm});
            skSolve(sketch);
        }
        {
            var Q0;
            {var subQ7=sQuery(id+"F12.wireOp",EDGE,"E72.0");var subQ14=sQuery(id+"F12.wireOp",EDGE,"E72.1");var subQ16=sQuery(id+"F12.wireOp",EDGE,"E74.1");var subQ18=sQuery(id+"F12.wireOp",EDGE,"E74.8");Q0=qUnion([makeQuery(id+"F12.imprint","IMPRINT",FACE,{"disambiguationData":[TD([[makeQuery(id+"F12.imprint","IMPRINT",EDGE,{"derivedFrom":subQ7}),1.0]])]}),makeQuery(id+"F12.imprint","IMPRINT",FACE,{"disambiguationData":[TD([[makeQuery(id+"F12.imprint","IMPRINT",EDGE,{"derivedFrom":subQ14}),1.0]])]}),makeQuery(id+"F12.imprint","IMPRINT",FACE,{"disambiguationData":[TD([[makeQuery(id+"F12.imprint","IMPRINT",EDGE,{"derivedFrom":subQ16}),1.0]])]}),makeQuery(id+"F12.imprint","IMPRINT",FACE,{"disambiguationData":[TD([[makeQuery(id+"F12.imprint","IMPRINT",EDGE,{"derivedFrom":subQ18}),-1.0]])]})]);}
            var Q1;
            Q1=makeQuery(id+"F5.boolean.opBoolean","SPLIT",FACE,{"disambiguationData":[TD([makeQuery(id+"F5.opExtrude","SWEPT_FACE",FACE,{"disambiguationData":[OSD([sQuery(id+"F4.wireOp",EDGE,"E41")])]})])],"derivedFrom":makeQuery(id+"F3.boolean.opBoolean","COPY",FACE,{"derivedFrom":makeQuery(id+"F3.opExtrude","CAP_FACE",FACE,{"disambiguationData":[OSD([sQuery(id+"F0.wireOp",EDGE,"E25.0"),sQuery(id+"F0.wireOp",EDGE,"E25.1"),sQuery(id+"F0.wireOp",EDGE,"E25.2"),sQuery(id+"F0.wireOp",EDGE,"E25.3"),sQuery(id+"F0.wireOp",EDGE,"E25.4"),sQuery(id+"F0.wireOp",EDGE,"E25.5"),sQuery(id+"F0.wireOp",EDGE,"E25.6"),sQuery(id+"F0.wireOp",EDGE,"E25.7")])],"isStart":false})})});
            extrude(context, id + "F13", {"entities" : qUnion([Q0]), "operationType" : NewBodyOperationType.REMOVE, "endBound" : BoundingType.UP_TO_SURFACE, "endBoundEntityFace" : qUnion([Q1]), "depth" : 25 * mm});
        }
        {
            var Q0;
            Q0=makeQuery(id+"F3.boolean.opBoolean","COPY",EDGE,{"derivedFrom":makeQuery(id+"F3.opExtrude","CAP_EDGE",EDGE,{"disambiguationData":[OSD([sQuery(id+"F0.wireOp",EDGE,"E25.6")])],"isStart":false})});
            var Q1;
            Q1=makeQuery(id+"F8.boolean.opBoolean","INTERSECT",EDGE,{"derivedFrom":[makeQuery(id+"F5.opExtrude","SWEPT_FACE",FACE,{"disambiguationData":[OSD([sQuery(id+"F4.wireOp",EDGE,"E30")])]}),makeQuery(id+"F8.opExtrude","CAP_FACE",FACE,{"disambiguationData":[OSD([sQuery(id+"F7.wireOp",EDGE,"E67")])],"isStart":false})]});
            var Q2;
            Q2=makeQuery(id+"F8.boolean.opBoolean","INTERSECT",EDGE,{"disambiguationData":[OD(1.0)],"derivedFrom":[makeQuery(id+"F5.opExtrude","SWEPT_FACE",FACE,{"disambiguationData":[OSD([sQuery(id+"F4.wireOp",EDGE,"E30")])]}),makeQuery(id+"F8.opExtrude","SWEPT_FACE",FACE,{"disambiguationData":[OSD([sQuery(id+"F7.wireOp",EDGE,"E67")])]})]});
            var Q3;
            {var subQ0=sQuery(id+"F4.wireOp",EDGE,"E30");Q3=makeQuery(id+"F8.boolean.opBoolean","SPLIT",EDGE,{"disambiguationData":[TD([makeQuery(id+"F5.opExtrude","SWEPT_FACE",FACE,{"disambiguationData":[OSD([sQuery(id+"F4.wireOp",EDGE,"E35.filletArc")])]})])],"derivedFrom":makeQuery(id+"F5.opExtrude","CAP_EDGE",EDGE,{"disambiguationData":[OSD([subQ0])],"isStart":false})});}
            var Q4;
            {var subQ0=sQuery(id+"F0.wireOp",EDGE,"E25.7");var subQ1=sQuery(id+"F0.wireOp",EDGE,"E25.1");var subQ2=sQuery(id+"F0.wireOp",EDGE,"E25.6");var subQ3=sQuery(id+"F0.wireOp",EDGE,"E25.5");var subQ4=sQuery(id+"F0.wireOp",EDGE,"E25.4");var subQ5=sQuery(id+"F0.wireOp",EDGE,"E25.0");var subQ6=sQuery(id+"F0.wireOp",EDGE,"E25.2");var subQ7=sQuery(id+"F0.wireOp",EDGE,"E25.3");Q4=makeQuery(id+"F8.boolean.opBoolean","INTERSECT",EDGE,{"derivedFrom":[makeQuery(id+"F5.boolean.opBoolean","SPLIT",FACE,{"disambiguationData":[TD([makeQuery(id+"F2.opExtrude","SWEPT_FACE",FACE,{"disambiguationData":[OSD([subQ5])]})])],"derivedFrom":makeQuery(id+"F3.boolean.opBoolean","COPY",FACE,{"derivedFrom":makeQuery(id+"F3.opExtrude","CAP_FACE",FACE,{"disambiguationData":[OSD([subQ5,subQ1,subQ6,subQ7,subQ4,subQ3,subQ2,subQ0])],"isStart":false})})}),makeQuery(id+"F8.opExtrude","SWEPT_FACE",FACE,{"disambiguationData":[OSD([sQuery(id+"F7.wireOp",EDGE,"E67")])]})]});}
            var Q5;
            Q5=makeQuery(id+"F8.boolean.opBoolean","INTERSECT",EDGE,{"disambiguationData":[OD(0.0)],"derivedFrom":[makeQuery(id+"F5.opExtrude","SWEPT_FACE",FACE,{"disambiguationData":[OSD([sQuery(id+"F4.wireOp",EDGE,"E30")])]}),makeQuery(id+"F8.opExtrude","SWEPT_FACE",FACE,{"disambiguationData":[OSD([sQuery(id+"F7.wireOp",EDGE,"E67")])]})]});
            fillet(context, id + "F14", {"entities" : qUnion([Q0, Q1, Q2, Q3, Q4, Q5]), "radius" : 3 * mm, "tangentPropagation" : true, "allowEdgeOverflow" : false});
        }
        {
            var Q0;
            Q0=makeQuery(id+"F1.opExtrude","CAP_EDGE",EDGE,{"disambiguationData":[OSD([sQuery(id+"F0.wireOp",EDGE,"E1.bottom")])],"isStart":false});
            fillet(context, id + "F15", {"entities" : qUnion([Q0]), "radius" : 2 * mm, "tangentPropagation" : true, "allowEdgeOverflow" : false});
        }
        {
            var Q0;
            {var subQ0=sQuery(id+"F0.wireOp",EDGE,"E21.filletArc");var subQ1=sQuery(id+"F0.wireOp",EDGE,"E7");var subQ2=sQuery(id+"F0.wireOp",EDGE,"E6");var subQ3=sQuery(id+"F0.wireOp",EDGE,"E5");var subQ4=sQuery(id+"F0.wireOp",EDGE,"E4");var subQ5=sQuery(id+"F0.wireOp",EDGE,"E22.filletArc");var subQ6=sQuery(id+"F0.wireOp",EDGE,"E1.bottom");var subQ7=sQuery(id+"F0.wireOp",EDGE,"E1.right");var subQ8=sQuery(id+"F0.wireOp",EDGE,"E1.top");var subQ9=sQuery(id+"F0.wireOp",EDGE,"E1.left");var subQ10=sQuery(id+"F0.wireOp",EDGE,"E23.filletArc");var subQ11=sQuery(id+"F0.wireOp",EDGE,"E24.filletArc");Q0=makeQuery(id+"F2.boolean.opBoolean","SPLIT",FACE,{"disambiguationData":[TD([makeQuery(id+"F1.opExtrude","SWEPT_FACE",FACE,{"disambiguationData":[OSD([subQ6])]})])],"derivedFrom":makeQuery(id+"F1.opExtrude","CAP_FACE",FACE,{"disambiguationData":[OSD([subQ6,subQ8,subQ9,subQ7,subQ4,subQ3,subQ2,subQ1,subQ0,subQ5,subQ10,subQ11])],"isStart":true})});}
            var sketch = newSketch(context, id + "F16", { "sketchPlane" : qUnion([Q0])});
            skLineSegment(sketch, "E79", {"start": v(0, 74.25) * mm, "end": v(0, 104.25) * mm, "construction": true});
            skCircle(sketch, "E80", {"center": v(0, 104.25) * mm, "radius": 6 * mm});
            skLineSegment(sketch, "E81", {"start": v(0, 104.25) * mm, "end": v(26.67, 104.25) * mm, "construction": true});
            skLineSegment(sketch, "E82", {"start": v(0, 104.25) * mm, "end": v(-15, 104.25) * mm, "construction": true});
            skLineSegment(sketch, "E83", {"start": v(-15, 104.25) * mm, "end": v(-15, 92.25) * mm});
            skLineSegment(sketch, "E84", {"start": v(-15, 92.25) * mm, "end": v(-33, 74.25) * mm});
            skArc(sketch, "E85", {"start": v(-15, 104.25) * mm, "mid": v(0, 119.25) * mm, "end": v(15, 104.25) * mm});
            skLineSegment(sketch, "E86", {"start": v(15, 104.25) * mm, "end": v(15, 92.25) * mm});
            skLineSegment(sketch, "E87", {"start": v(15, 92.25) * mm, "end": v(33, 74.25) * mm});
            skLineSegment(sketch, "E88", {"start": v(-74.25, 0) * mm, "end": v(74.25, 0) * mm, "construction": true});
            skLineSegment(sketch, "E89.MirrorCS", {"start": v(-15, -92.25) * mm, "end": v(-33, -74.25) * mm});
            skLineSegment(sketch, "E90.MirrorCS", {"start": v(-15, -104.25) * mm, "end": v(-15, -92.25) * mm});
            skArc(sketch, "E91.MirrorCS", {"start": v(-15, -104.25) * mm, "mid": v(0, -119.25) * mm, "end": v(15, -104.25) * mm});
            skCircle(sketch, "E92.MirrorC", {"center": v(0, -104.25) * mm, "radius": 6 * mm});
            skLineSegment(sketch, "E93.MirrorCS", {"start": v(15, -104.25) * mm, "end": v(15, -92.25) * mm});
            skLineSegment(sketch, "E94.MirrorCS", {"start": v(15, -92.25) * mm, "end": v(33, -74.25) * mm});
            skSolve(sketch);
        }
        {
            var Q0;
            Q0=makeQuery(id+"F16.imprint","IMPRINT",FACE,{"disambiguationData":[TD([[makeQuery(id+"F16.imprint","IMPRINT",EDGE,{"derivedFrom":makeQuery(id+"F1.opExtrude","CAP_EDGE",EDGE,{"disambiguationData":[OSD([sQuery(id+"F0.wireOp",EDGE,"E1.left")])],"isStart":true})}),-1.0]])]});
            var Q1;
            Q1=makeQuery(id+"F16.imprint","IMPRINT",FACE,{"disambiguationData":[TD([[makeQuery(id+"F16.imprint","IMPRINT",EDGE,{"derivedFrom":sQuery(id+"F16.wireOp",EDGE,"E80")}),-1.0]])]});
            var Q2;
            {var subQ0=sQuery(id+"F16.wireOp",EDGE,"E89.MirrorCS");Q2=makeQuery(id+"F16.imprint","IMPRINT",FACE,{"disambiguationData":[TD([[makeQuery(id+"F16.imprint","IMPRINT",EDGE,{"derivedFrom":subQ0}),-1.0]])]});}
            var Q3;
            Q3=makeQuery(id+"F2.opExtrude","CAP_FACE",FACE,{"disambiguationData":[OSD([sQuery(id+"F0.wireOp",EDGE,"E12"),sQuery(id+"F0.wireOp",EDGE,"E13"),sQuery(id+"F0.wireOp",EDGE,"E14"),sQuery(id+"F0.wireOp",EDGE,"E15"),sQuery(id+"F0.wireOp",EDGE,"E17.filletArc"),sQuery(id+"F0.wireOp",EDGE,"E18.filletArc"),sQuery(id+"F0.wireOp",EDGE,"E19.filletArc"),sQuery(id+"F0.wireOp",EDGE,"E20.filletArc"),sQuery(id+"F0.wireOp",EDGE,"E25.0"),sQuery(id+"F0.wireOp",EDGE,"E25.1"),sQuery(id+"F0.wireOp",EDGE,"E25.2"),sQuery(id+"F0.wireOp",EDGE,"E25.3"),sQuery(id+"F0.wireOp",EDGE,"E25.4"),sQuery(id+"F0.wireOp",EDGE,"E25.5"),sQuery(id+"F0.wireOp",EDGE,"E25.6"),sQuery(id+"F0.wireOp",EDGE,"E25.7")])],"isStart":false});
            extrude(context, id + "F17", {"entities" : qUnion([Q0, Q1, Q2]), "endBound" : BoundingType.UP_TO_SURFACE, "depth" : 25 * mm, "endBoundEntityFace" : qUnion([Q3]), "offsetDistance" : 25 * mm});
        }
    });
